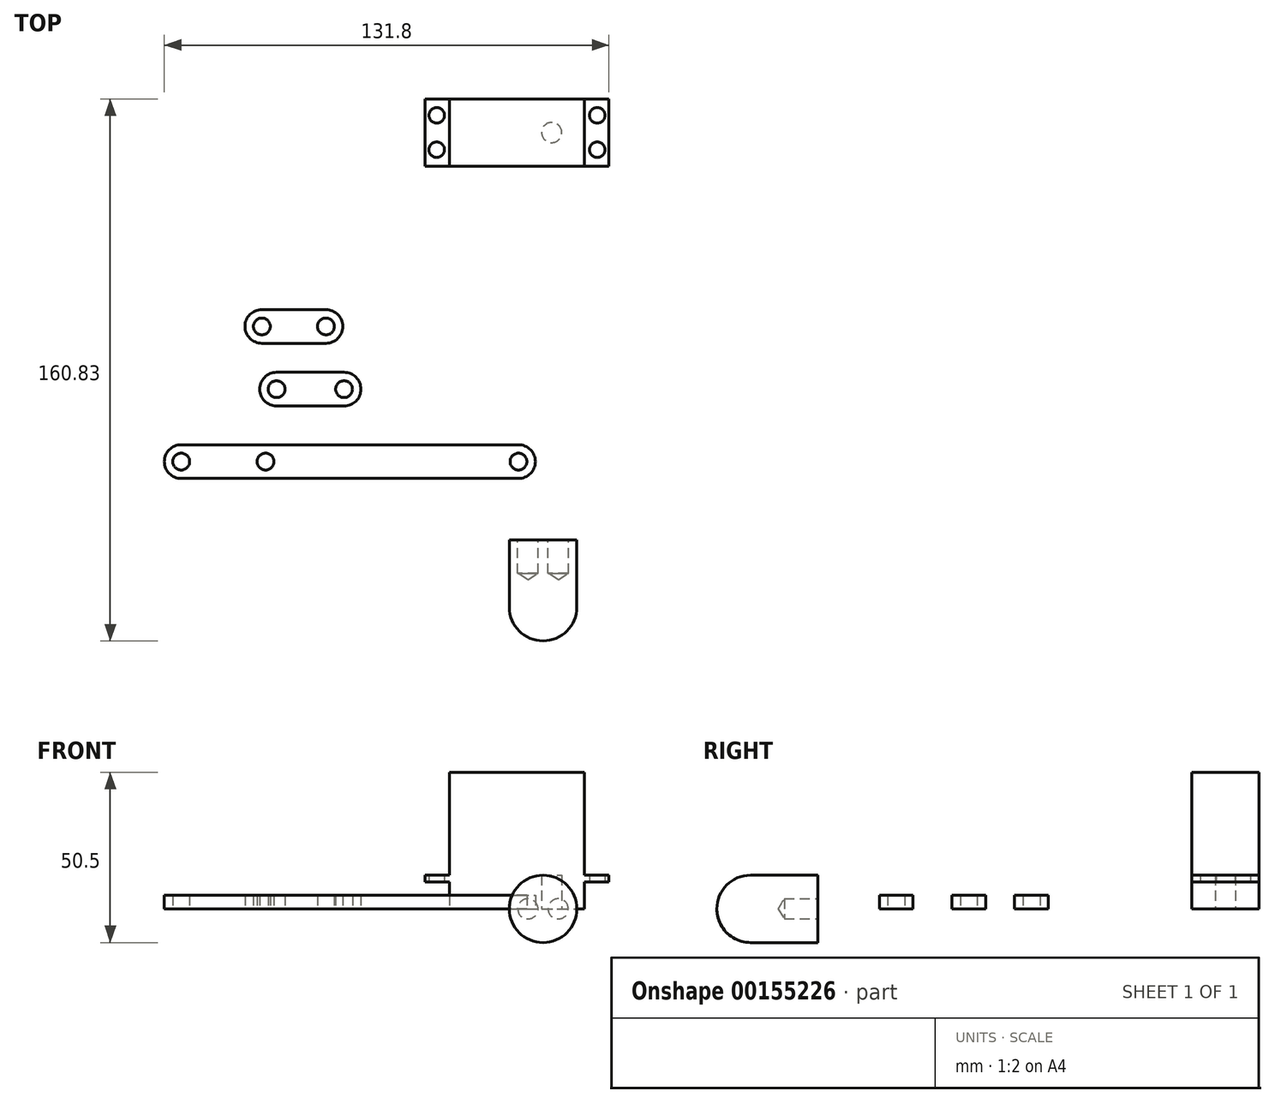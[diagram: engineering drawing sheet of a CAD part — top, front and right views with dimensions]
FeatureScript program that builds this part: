
annotation { "Feature Type Name" : "Feature", "Feature Type Description" : "" }
export const myFeature = defineFeature(function(context is Context, id is Id, definition is map)
    precondition{}
    {
        {
            var Q0;
            Q0=qCreatedBy(makeId("Front.planeOp"),FACE);
            var sketch = newSketch(context, id + "F0", { "sketchPlane" : qUnion([Q0])});
            skCircle(sketch, "E0", {"center": v(0, 0) * mm, "radius": 10 * mm});
            skSolve(sketch);
        }
        {
            var Q0;
            Q0=makeQuery(id+"F0.imprint","IMPRINT",FACE,{"disambiguationData":[TD([[makeQuery(id+"F0.imprint","IMPRINT",EDGE,{"derivedFrom":sQuery(id+"F0.wireOp",EDGE,"E0")}),1.0]])]});
            extrude(context, id + "F1", {"entities" : qUnion([Q0]), "depth" : 30 * mm});
        }
        {
            var Q0;
            Q0=makeQuery(id+"F1.opExtrude","CAP_EDGE",EDGE,{"disambiguationData":[OSD([sQuery(id+"F0.wireOp",EDGE,"E0")])],"isStart":false});
            fillet(context, id + "F2", {"entities" : qUnion([Q0]), "radius" : 10 * mm, "tangentPropagation" : true, "allowEdgeOverflow" : false});
        }
        {
            var Q0;
            Q0=makeQuery(id+"F1.opExtrude","CAP_FACE",FACE,{"disambiguationData":[OSD([sQuery(id+"F0.wireOp",EDGE,"E0")])],"isStart":true});
            var sketch = newSketch(context, id + "F3", { "sketchPlane" : qUnion([Q0])});
            skCircle(sketch, "E1", {"center": v(-4.5, 0) * mm, "radius": 3 * mm});
            skCircle(sketch, "E2", {"center": v(4.5, 0) * mm, "radius": 3 * mm});
            skSolve(sketch);
        }
        {
            var Q0;
            Q0=sQuery(id+"F3.wireOp",VERTEX,"E1.center");
            var Q1;
            Q1=sQuery(id+"F3.wireOp",VERTEX,"E2.center");
            var Q2;
            Q2=makeQuery(id+"F1.opExtrude","SWEPT_BODY",BODY,{"disambiguationData":[OSD([sQuery(id+"F0.wireOp",EDGE,"E0")])]});
            hole(context, id + "F4", {"style" : HoleStyle.SIMPLE, "endStyle" : HoleEndStyle.BLIND, "holeDiameter" : 6 * mm, "holeDepth" : 10 * mm, "locations" : qUnion([Q0, Q1]), "scope" : qUnion([Q2])});
        }
        {
            assignVariable(context, id + "F5", {"name" : "motz", "anyValue" : 40.5});
        }
        {
            assignVariable(context, id + "F6", {"name" : "mottox", "anyValue" : 54.5});
        }
        {
            var Q0;
            Q0=qCreatedBy(makeId("Top.planeOp"),FACE);
            var sketch = newSketch(context, id + "F7", { "sketchPlane" : qUnion([Q0])});
            skLineSegment(sketch, "E3.bottom", {"start": v(-27.73, 130.83) * mm, "end": v(12.27, 130.83) * mm});
            skLineSegment(sketch, "E3.top", {"start": v(-27.73, 110.83) * mm, "end": v(12.27, 110.83) * mm});
            skLineSegment(sketch, "E3.left", {"start": v(-27.73, 130.83) * mm, "end": v(-27.73, 110.83) * mm});
            skLineSegment(sketch, "E3.right", {"start": v(12.27, 130.83) * mm, "end": v(12.27, 110.83) * mm});
            skSolve(sketch);
        }
        {
            var Q0;
            Q0=makeQuery(id+"F7.imprint","IMPRINT",FACE,{"disambiguationData":[TD([[makeQuery(id+"F7.imprint","IMPRINT",EDGE,{"derivedFrom":sQuery(id+"F7.wireOp",EDGE,"E3.bottom")}),-1.0]])]});
            extrude(context, id + "F8", {"entities" : qUnion([Q0]), "depth" : (getVariable(context, 'motz')) * mm});
        }
        {
            var Q0;
            Q0=makeQuery(id+"F8.opExtrude","SWEPT_FACE",FACE,{"disambiguationData":[OSD([sQuery(id+"F7.wireOp",EDGE,"E3.left")])]});
            cPlane(context, id + "F9", {"entities" : qUnion([Q0]), "cplaneType" : CPlaneType.OFFSET, "offset" : (20) * mm, "oppositeDirection" : true, "width" : 150 * mm, "height" : 150 * mm});
        }
        {
            var Q0;
            Q0=qCreatedBy(id+"F9.planeOp",FACE);
            var sketch = newSketch(context, id + "F10", { "sketchPlane" : qUnion([Q0])});
            skLineSegment(sketch, "E4.bottom", {"start": v(-130.83, 8) * mm, "end": v(-110.83, 8) * mm});
            skLineSegment(sketch, "E4.top", {"start": v(-130.83, 10) * mm, "end": v(-110.83, 10) * mm});
            skLineSegment(sketch, "E4.left", {"start": v(-130.83, 8) * mm, "end": v(-130.83, 10) * mm});
            skLineSegment(sketch, "E4.right", {"start": v(-110.83, 8) * mm, "end": v(-110.83, 10) * mm});
            skSolve(sketch);
        }
        {
            var Q0;
            Q0 = qSketchRegion(id + "F10", true);
            extrude(context, id + "F11", {"entities" : qUnion([Q0]), "operationType" : NewBodyOperationType.ADD, "endBound" : BoundingType.SYMMETRIC, "depth" : (getVariable(context, 'mottox')) * mm});
        }
        {
            var Q0;
            Q0=makeQuery(id+"F8.opExtrude","CAP_FACE",FACE,{"disambiguationData":[OSD([sQuery(id+"F7.wireOp",EDGE,"E3.bottom"),sQuery(id+"F7.wireOp",EDGE,"E3.top"),sQuery(id+"F7.wireOp",EDGE,"E3.left"),sQuery(id+"F7.wireOp",EDGE,"E3.right")])],"isStart":true});
            var sketch = newSketch(context, id + "F12", { "sketchPlane" : qUnion([Q0])});
            skLineSegment(sketch, "E5", {"start": v(12.27, -120.83) * mm, "end": v(-27.73, -120.83) * mm, "construction": true});
            skCircle(sketch, "E6", {"center": v(2.57, -120.83) * mm, "radius": 3 * mm});
            skSolve(sketch);
        }
        {
            var Q0;
            Q0 = qSketchRegion(id + "F12", true);
            extrude(context, id + "F13", {"entities" : qUnion([Q0]), "operationType" : NewBodyOperationType.REMOVE, "oppositeDirection" : true, "depth" : 10 * mm});
        }
        {
            var Q0;
            {var subQ2=sQuery(id+"F10.wireOp",EDGE,"E4.bottom");Q0=makeQuery(id+"F11.boolean.opBoolean","SPLIT",FACE,{"disambiguationData":[TD([makeQuery(id+"F8.opExtrude","SWEPT_FACE",FACE,{"disambiguationData":[OSD([sQuery(id+"F7.wireOp",EDGE,"E3.right")])]})])],"derivedFrom":makeQuery(id+"F11.opExtrude","SWEPT_FACE",FACE,{"disambiguationData":[OSD([subQ2])]})});}
            var sketch = newSketch(context, id + "F14", { "sketchPlane" : qUnion([Q0])});
            skCircle(sketch, "E7", {"center": v(16.07, -115.73) * mm, "radius": 2.3 * mm});
            skCircle(sketch, "E8", {"center": v(16.07, -125.93) * mm, "radius": 2.3 * mm});
            skLineSegment(sketch, "E9", {"start": v(-7.73, -110.83) * mm, "end": v(-7.73, -130.83) * mm, "construction": true});
            skCircle(sketch, "E10.MirrorC", {"center": v(-31.53, -125.93) * mm, "radius": 2.3 * mm});
            skCircle(sketch, "E11.MirrorC", {"center": v(-31.53, -115.73) * mm, "radius": 2.3 * mm});
            skSolve(sketch);
        }
        {
            var Q0;
            Q0 = qSketchRegion(id + "F14", true);
            extrude(context, id + "F15", {"entities" : qUnion([Q0]), "operationType" : NewBodyOperationType.REMOVE, "oppositeDirection" : true, "depth" : 3 * mm});
        }
        {
            var Q0;
            Q0=qCreatedBy(makeId("Top.planeOp"),FACE);
            var sketch = newSketch(context, id + "F16", { "sketchPlane" : qUnion([Q0])});
            skCircle(sketch, "E12", {"center": v(-79, 44.69) * mm, "radius": 5 * mm});
            skLineSegment(sketch, "E13.bottom", {"start": v(-79, 49.69) * mm, "end": v(-59, 49.69) * mm});
            skLineSegment(sketch, "E13.top", {"start": v(-79, 39.69) * mm, "end": v(-59, 39.69) * mm});
            skLineSegment(sketch, "E13.left", {"start": v(-79, 49.69) * mm, "end": v(-79, 39.69) * mm});
            skLineSegment(sketch, "E13.right", {"start": v(-59, 49.69) * mm, "end": v(-59, 39.69) * mm});
            skCircle(sketch, "E14", {"center": v(-59, 44.69) * mm, "radius": 5 * mm});
            skCircle(sketch, "E15", {"center": v(-79, 44.69) * mm, "radius": 2.5 * mm});
            skCircle(sketch, "E16", {"center": v(-59, 44.69) * mm, "radius": 2.5 * mm});
            skSolve(sketch);
        }
        {
            var Q0;
            Q0 = qSketchRegion(id + "F16", true);
            extrude(context, id + "F17", {"entities" : qUnion([Q0]), "depth" : 4 * mm});
        }
        {
            var Q0;
            Q0=qCreatedBy(makeId("Top.planeOp"),FACE);
            var sketch = newSketch(context, id + "F18", { "sketchPlane" : qUnion([Q0])});
            skCircle(sketch, "E17", {"center": v(-107.28, 23.2) * mm, "radius": 5 * mm});
            skLineSegment(sketch, "E18.bottom", {"start": v(-107.28, 28.2) * mm, "end": v(-7.28, 28.2) * mm});
            skLineSegment(sketch, "E18.top", {"start": v(-107.28, 18.2) * mm, "end": v(-7.28, 18.2) * mm});
            skLineSegment(sketch, "E18.left", {"start": v(-107.28, 28.2) * mm, "end": v(-107.28, 18.2) * mm});
            skLineSegment(sketch, "E18.right", {"start": v(-7.28, 28.2) * mm, "end": v(-7.28, 18.2) * mm});
            skCircle(sketch, "E19", {"center": v(-7.28, 23.2) * mm, "radius": 5 * mm});
            skCircle(sketch, "E20", {"center": v(-107.28, 23.2) * mm, "radius": 2.5 * mm});
            skCircle(sketch, "E21", {"center": v(-82.28, 23.2) * mm, "radius": 2.5 * mm});
            skCircle(sketch, "E22", {"center": v(-7.28, 23.2) * mm, "radius": 2.5 * mm});
            skSolve(sketch);
        }
        {
            var Q0;
            Q0 = qSketchRegion(id + "F18", true);
            extrude(context, id + "F19", {"entities" : qUnion([Q0]), "depth" : 4 * mm});
        }
        {
            var Q0;
            Q0=qCreatedBy(makeId("Top.planeOp"),FACE);
            var sketch = newSketch(context, id + "F20", { "sketchPlane" : qUnion([Q0])});
            skCircle(sketch, "E23", {"center": v(-83.37, 63.3) * mm, "radius": 5 * mm});
            skCircle(sketch, "E24", {"center": v(-64.37, 63.3) * mm, "radius": 5 * mm});
            skLineSegment(sketch, "E25.bottom", {"start": v(-83.37, 68.3) * mm, "end": v(-64.37, 68.3) * mm});
            skLineSegment(sketch, "E25.top", {"start": v(-83.37, 58.3) * mm, "end": v(-64.37, 58.3) * mm});
            skLineSegment(sketch, "E25.left", {"start": v(-83.37, 68.3) * mm, "end": v(-83.37, 58.3) * mm});
            skLineSegment(sketch, "E25.right", {"start": v(-64.37, 68.3) * mm, "end": v(-64.37, 58.3) * mm});
            skCircle(sketch, "E26", {"center": v(-83.37, 63.3) * mm, "radius": 2.5 * mm});
            skCircle(sketch, "E27", {"center": v(-64.37, 63.3) * mm, "radius": 2.5 * mm});
            skSolve(sketch);
        }
        {
            var Q0;
            Q0 = qSketchRegion(id + "F20", true);
            extrude(context, id + "F21", {"entities" : qUnion([Q0]), "depth" : 4 * mm});
        }
    });
